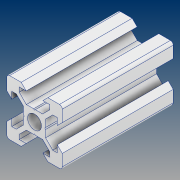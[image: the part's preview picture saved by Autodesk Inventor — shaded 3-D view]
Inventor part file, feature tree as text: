
AUTODESK INVENTOR PART (.ipt)
format: ipt  version: 2021 (Build 250183000, 183)  size: 192,512 bytes
history: native  units: mm
features: extrude x1, sketch x1
ambient origin geometry x8: Origin, YZ Plane, XZ Plane, XY Plane, X Axis, Y Axis, Z Axis, Center Point
bodies: Solid1 (feature_tree)
feature tree (2):
  extrude  "Extrusion1"  Depth=40.0mm TaperAngle=0.0deg
  sketch  "Sketch1"  dims[d1=40.0mm d2=360.0deg d3=40.0mm d4=0.0mm]
